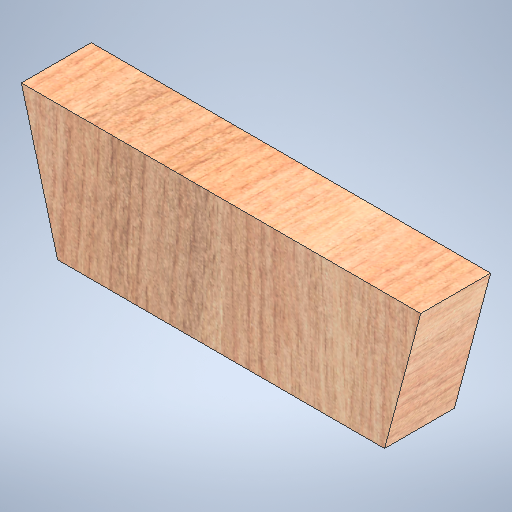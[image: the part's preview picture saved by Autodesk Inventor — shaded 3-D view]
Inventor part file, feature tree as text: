
AUTODESK INVENTOR PART (.ipt)
format: ipt  version: 2025 (Build 290162000, 162)  size: 442,368 bytes
history: native  units: in
note: dims shown in document units (in); Inventor stores cm internally (conversion verified against a paired STEP export)
features: extrude x1, sketch x1
ambient origin geometry x8: Origin, YZ Plane, XZ Plane, XY Plane, X Axis, Y Axis, Z Axis, Center Point
bodies: Solid1 (feature_tree)
feature tree (2):
  extrude  "Extrusion1"  Depth=4.0in
  sketch  "Sketch1"  dims[d0=11.428in d1=4.0in d2=75.0deg d3=4.0in d4=75.0deg d5=2.0in d6=0.0in]
